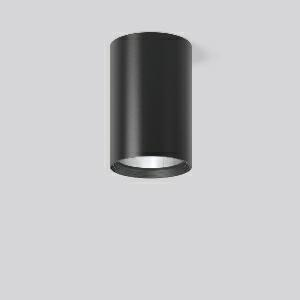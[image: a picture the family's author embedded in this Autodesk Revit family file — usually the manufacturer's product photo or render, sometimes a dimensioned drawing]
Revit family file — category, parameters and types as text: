
# Revit family: heledon_maxi_a_931231_003_76_1986
name_source: partatom
category: Lighting Fixtures
units: mm (PartAtom-declared; Revit-internal decimal feet)

## family parameters
Cut with Voids When Loaded = No
Host = Face
Light Source = No
Part Type = Normal
Room Calculation Point = No
Round Connector Dimension = Use Diameter
Shared = No

## types (1)
- HELEDON maxi A (1 x LED Modul 932 fresh meat, 2150 lm, 3200)
    Apparent Load = 33 VA
    Approval mark = CE
    CIE Flux Codes = 100 100 100 100 100
    Color Rendering = 90
    Color Temperature = 3200
    Default Elevation = 1800 mm
    Description = Series: HELEDON maxi
Cylindrical surface-mounted downlight. Housing: die-cast aluminium, powder-coated. Internal ceiling frame polycarbonate with bayonet mounting. Black plastic ring and recessed LED to prevent glare from the side. Optical assembly with reflector made of MIRO-Silver with 98% total light reflection for outstanding efficiency - can be changed without tools. Special LED for illumination of meat included. Suitable for Ceiling mounting. Easy installation with a separate ceiling frame with bayonet mounting and plug connection. Driver integrated. Connected via plug-in connector. High quality converter without flickering and stroboscopic effect. The following accessories can be mounted without use of tools: interchangeable lenses, decorative glasses, honeycomb louvre, clear and frosted diffusers, white interchangeable plastic ring. 
Colour: deep black, matt (RAL 9005)
Diameter: 123 mm
Height: 183 mm
Lamp: LED
Socket: without socket
Colour temperature: fresh meat
System power: 33 W
Rated luminous flux: 2150 lm
Luminous efficiency: 65 lm/W
Control gear: Converter, dimmable, DALI
Protection class: I
Type of protection: IP 20
    Height = 183 mm
    Lamp = 1 x LED Modul 932 fresh meat
    Lamp Light Flux = 2150 lm
    Lamp count = 1
    Length = 123 mm
    Lifetime = 50000 h
    Luminous efficacy = 65 lm/W
    Manufacturer = RZB
    ModVariant = No
    Model = 931231.003.76
    Mounting Place = Ceiling
    Mounting Type = Surface mounted
    Number of Poles = 1
    OnlyDefault = Yes
    Power Factor = 1
    Product Name = HELEDON maxi A
    Product group = Surface mounted downlights
    ProductGroupID = 302
    Protection Class = Protection class I
    Protection Degree = IP 20
    RLX_Detail_Level = 1
    RLX_Emergency_Light_Flux = 0 lm
    RLX_Emergency_Type = 0
    RLX_Emergency_Type_DB = No
    RlxData = <blob elided: 98945 chars, md5=93d11009>
    Socket = socket
    Standby Power = 0 W
    System Light Flux = 2150 lm
    System Power = 33 W
    Type Comments = Product without accessories
    Type Image = 931192.003.jpg
    URL = http://relux.com
    VarID = ---
    Voltage = 230 V
    Voltage Range = 220-240 V
    Weight = 0.00 kg
    Width = 0 mm  [stored 0 ft]

note: [stored X ft] marks values corroborated as IEEE doubles in the binary element streams (Revit-internal decimal feet)

## geometry (parser evidence)
native form markers: Blend x4, Sweep x11
no freeform markers — native parametric forms only
